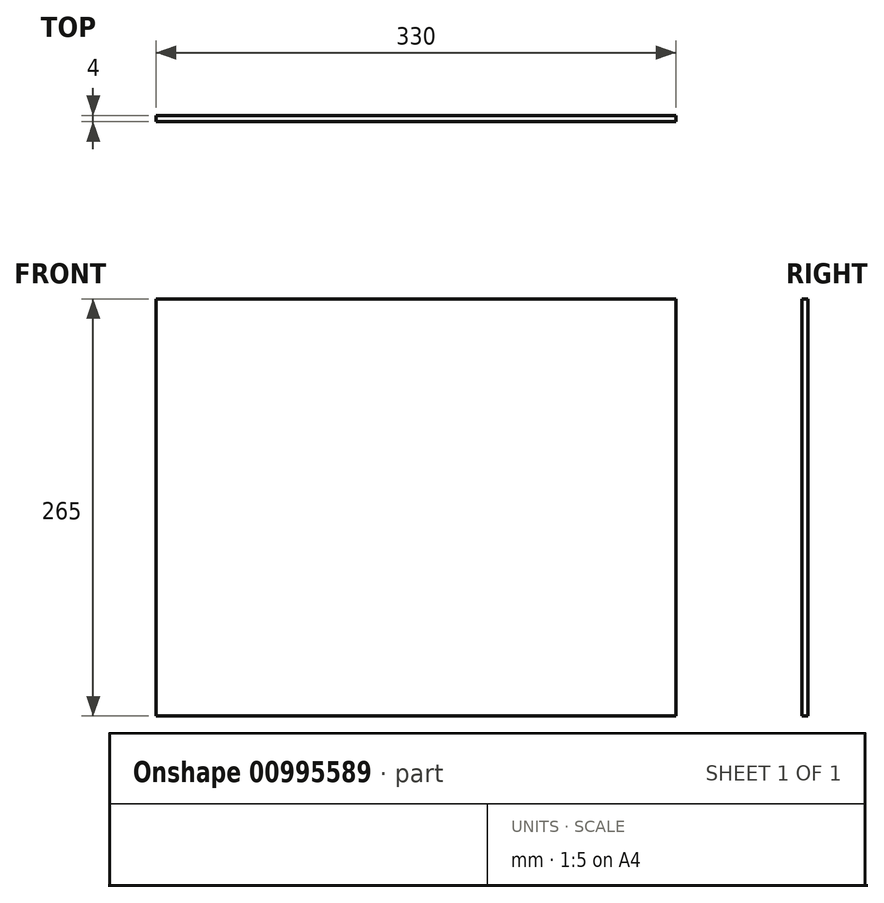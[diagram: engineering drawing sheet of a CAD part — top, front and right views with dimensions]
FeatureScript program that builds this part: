
annotation { "Feature Type Name" : "Feature", "Feature Type Description" : "" }
export const myFeature = defineFeature(function(context is Context, id is Id, definition is map)
    precondition{}
    {
        {
            var Q0;
            Q0=qCreatedBy(makeId("Front.planeOp"),FACE);
            var sketch = newSketch(context, id + "F0", { "sketchPlane" : qUnion([Q0])});
            skLineSegment(sketch, "E0.bottom", {"start": v(0, 0) * mm, "end": v(330, 0) * mm});
            skLineSegment(sketch, "E0.top", {"start": v(0, 265) * mm, "end": v(330, 265) * mm});
            skLineSegment(sketch, "E0.left", {"start": v(0, 0) * mm, "end": v(0, 265) * mm});
            skLineSegment(sketch, "E0.right", {"start": v(330, 0) * mm, "end": v(330, 265) * mm});
            skSolve(sketch);
        }
        {
            var Q0;
            Q0 = qSketchRegion(id + "F0", true);
            extrude(context, id + "F1", {"entities" : qUnion([Q0]), "depth" : 4 * mm, "offsetDistance" : 25 * mm});
        }
    });
